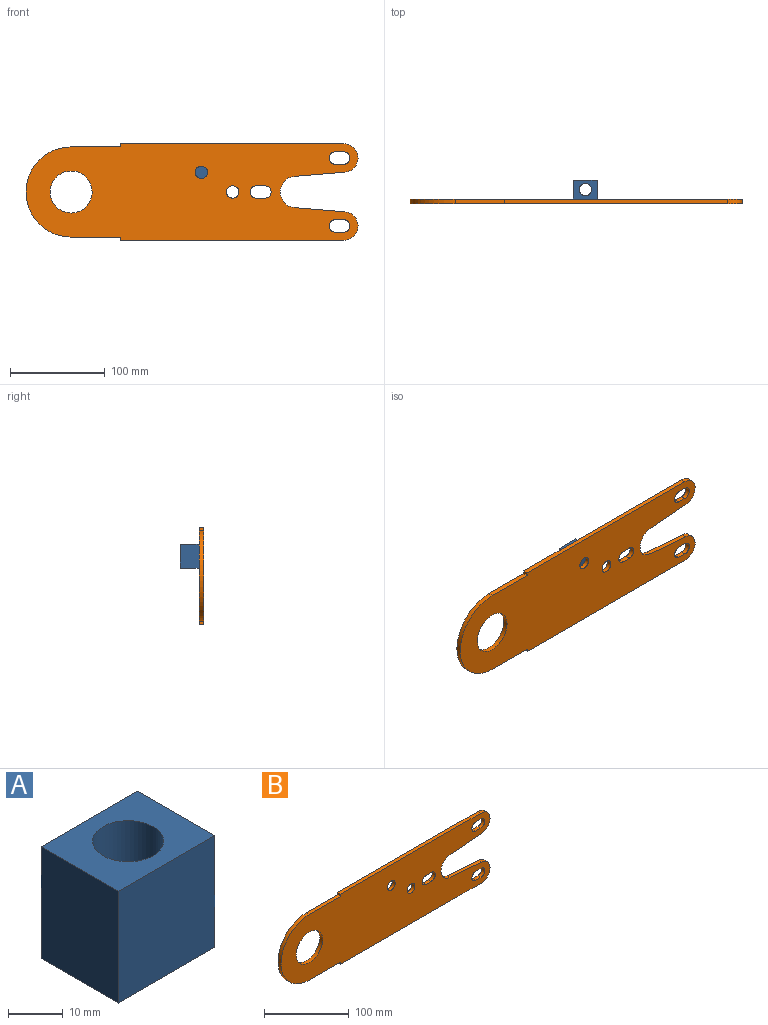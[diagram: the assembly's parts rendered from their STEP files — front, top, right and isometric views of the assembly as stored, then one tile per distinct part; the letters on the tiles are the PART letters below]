
ASSEMBLY  parts=2 mates=1
PART A: 7 faces, bbox 25x20x25 mm
  f0: plane 25x20mm, normal (1,0,0), area 500mm2, adj f1,f3,f4,f5
  f1: plane 25x20mm, normal (0,0,1), area 367.3mm2, adj f0,f2,f4,f5,f6
  f2: plane 25x20mm, normal (-1,0,0), area 500mm2, adj f1,f3,f4,f5
  f3: plane 25x20mm, normal (0,0,-1), area 367.3mm2, adj f0,f2,f4,f5,f6
  f4: plane 25x25mm, normal (0,-1,0), area 625mm2, adj f0,f1,f2,f3
  f5: plane 25x25mm, normal (0,1,0), area 625mm2, adj f0,f1,f2,f3
  f6: cylinder r=6.5mm len=25mm, axis (0,0,1), area 1021mm2, adj f1,f3
PART B: 29 faces, bbox 349.6x5x101.5 mm
  f0: cylinder r=6.5mm len=13mm, axis (0,1,0), area 102.1mm2, adj f1,f26,f27,f28
  f1: plane 9x5mm, normal (0,0,-1), area 45mm2, adj f0,f2,f27,f28
  f2: cylinder r=6.5mm len=13mm, axis (0,1,0), area 102.1mm2, adj f1,f26,f27,f28
  f3: cylinder r=6.5mm len=13mm, axis (0,1,0), area 102.1mm2, adj f4,f20,f27,f28
  f4: plane 9x5mm, normal (0,0,-1), area 45mm2, adj f3,f5,f27,f28
  f5: cylinder r=6.5mm len=13mm, axis (0,1,0), area 102.1mm2, adj f4,f20,f27,f28
  f6: plane 52.13x5mm, normal (0,0,1), area 260.6mm2, adj f7,f24,f27,f28
  f7: cylinder r=47.5mm len=95mm, axis (0,1,0), area 746.1mm2, adj f6,f8,f27,f28
  f8: plane 52.13x5mm, normal (0,0,-1), area 260.6mm2, adj f7,f9,f27,f28
  f9: plane 5x3.25mm, normal (-1,0,0), area 16.3mm2, adj f8,f10,f27,f28
  f10: plane 235x5mm, normal (0,0,-1), area 1175mm2, adj f9,f11,f27,f28
  f11: cylinder r=15mm len=29.95mm, axis (0,1,0), area 229.5mm2, adj f10,f12,f27,f28
  f12: plane 53.08x5mm, normal (0.08,0,1), area 266.3mm2, adj f11,f13,f27,f28
  f13: cylinder r=16.5mm len=32.89mm, axis (0,1,0), area 245.7mm2, adj f12,f14,f27,f28
  f14: plane 53.08x5mm, normal (0.08,0,-1), area 266.3mm2, adj f13,f15,f27,f28
  f15: cylinder r=15mm len=29.95mm, axis (0,1,0), area 229.5mm2, adj f14,f16,f27,f28
  f16: plane 235x5mm, normal (0,0,1), area 1175mm2, adj f15,f24,f27,f28
  f17: plane 9x5mm, normal (0,0,1), area 45mm2, adj f18,f25,f27,f28
  f18: cylinder r=6.5mm len=13mm, axis (0,1,0), area 102.1mm2, adj f17,f19,f27,f28
  f19: plane 9x5mm, normal (0,0,-1), area 45mm2, adj f18,f25,f27,f28
  f20: plane 9x5mm, normal (0,0,1), area 45mm2, adj f3,f5,f27,f28
  f21: cylinder r=6.5mm len=13mm, axis (0,1,0), area 204.2mm2, adj f27,f28
  f22: cylinder r=6.5mm len=13mm, axis (0,1,0), area 204.2mm2, adj f27,f28
  f23: cylinder r=22.12mm len=44.25mm, axis (0,1,0), area 695.1mm2, adj f27,f28
  f24: plane 5x3.25mm, normal (-1,0,0), area 16.3mm2, adj f6,f16,f27,f28
  f25: cylinder r=6.5mm len=13mm, axis (0,1,0), area 102.1mm2, adj f17,f19,f27,f28
  f26: plane 9x5mm, normal (0,0,1), area 45mm2, adj f0,f2,f27,f28
  f27: plane 349.63x101.5mm, normal (0,-1,0), area 28193.8mm2, adj f0,f1,f2,f3,f4,f5,f6,f7
  f28: plane 349.63x101.5mm, normal (0,1,0), area 28193.8mm2, adj f0,f1,f2,f3,f4,f5,f6,f7
PLACE A rot(axis=(1,0,0),180deg) t=(86.02,40.92,12.38)mm
PLACE B t=(-51.1,40.92,-8.37)mm
MATE fastened A.f5 <-> B.f22  axis (0,-1,0) through (86.02,40.92,12.38)mm
